# Revit family: Columns_&_Screens-Teknion-RPSWG_Worksurface_Edge_Screen-R2019
name_source: partatom
category: Furniture
units: mm (PartAtom-declared; Revit-internal decimal feet)

## family parameters
Always vertical = Yes
Cut with Voids When Loaded = No
OmniClass Number = 23.40.20.00
OmniClass Title = General Furniture and Specialties
Room Calculation Point = No
Shared = Yes
Work Plane-Based = No

## types (2) — shared parameters
Assembly Code = E2020200
Manufacturer = Teknion
Manufacturer Fax = 416.661.4586
Part Number = RPSWG
Product Documentation Link = https://www.teknion.com
Product Line = Expansion Desking
Product Page URL = https://www.teknion.com
Series = Expansion Desking
Sustainability Data = https://www.teknion.com
URL = www.teknion.com
Unit Weight URL = http://www.teknion.com
Warranty = http://www.teknion.com

## per-type parameters (varying)
| type | Description | Height | Model |
| 42" High Datum Line | Worksurface Edge Screen - Glass, 42" High Datum Line | 42 " | RPSWG13__ |
| 51" High Datum Line | Worksurface Edge Screen - Glass, 51" High Datum Line | 50.831 " | RPSWG22__ |

## geometry (parser evidence)
native form markers: Sweep x3
no freeform markers — native parametric forms only
